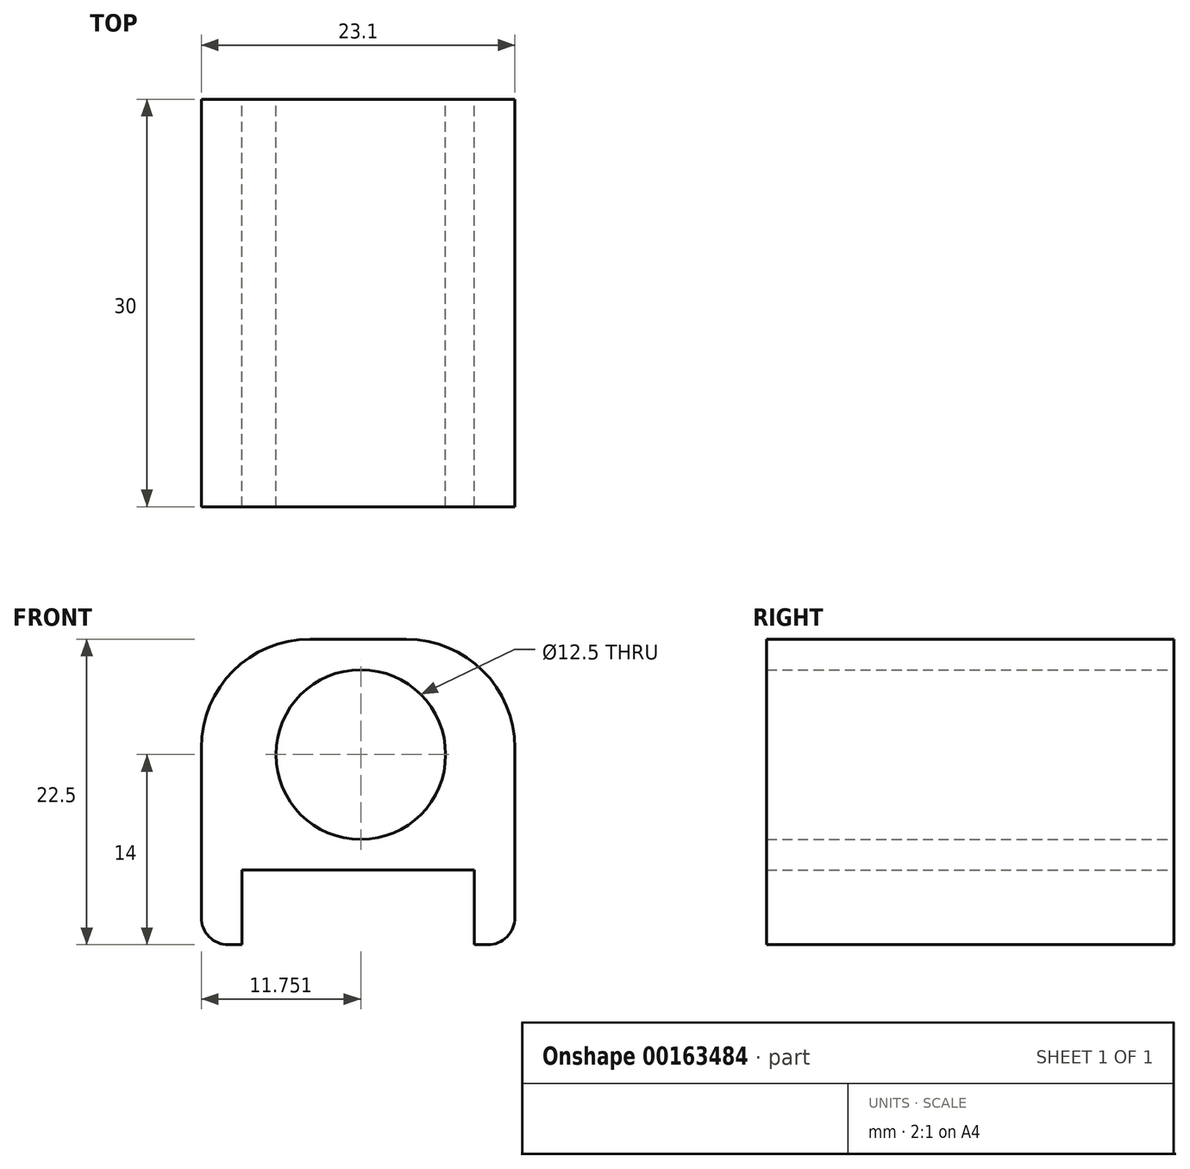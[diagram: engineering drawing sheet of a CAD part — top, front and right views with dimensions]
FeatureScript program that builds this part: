
annotation { "Feature Type Name" : "Feature", "Feature Type Description" : "" }
export const myFeature = defineFeature(function(context is Context, id is Id, definition is map)
    precondition{}
    {
        {
            var Q0;
            Q0=qCreatedBy(makeId("Front.planeOp"),FACE);
            var sketch = newSketch(context, id + "F0", { "sketchPlane" : qUnion([Q0])});
            skLineSegment(sketch, "E0.bottom", {"start": v(-11.26, 17) * mm, "end": v(-4.16, 17) * mm});
            skLineSegment(sketch, "E0.top", {"start": v(-19.26, 0) * mm, "end": v(3.84, 0) * mm});
            skLineSegment(sketch, "E0.left", {"start": v(-19.26, 9) * mm, "end": v(-19.26, 0) * mm});
            skLineSegment(sketch, "E0.right", {"start": v(3.84, 9) * mm, "end": v(3.84, 0) * mm});
            skLineSegment(sketch, "E1.bottom", {"start": v(-19.26, 0) * mm, "end": v(-16.26, 0) * mm});
            skLineSegment(sketch, "E1.top", {"start": v(-17.26, -5.5) * mm, "end": v(-16.26, -5.5) * mm});
            skLineSegment(sketch, "E1.left", {"start": v(-19.26, 0) * mm, "end": v(-19.26, -3.5) * mm});
            skLineSegment(sketch, "E1.right", {"start": v(-16.26, 0) * mm, "end": v(-16.26, -5.5) * mm});
            skLineSegment(sketch, "E2.bottom", {"start": v(3.84, 0) * mm, "end": v(0.84, 0) * mm});
            skLineSegment(sketch, "E2.top", {"start": v(1.84, -5.5) * mm, "end": v(0.84, -5.5) * mm});
            skLineSegment(sketch, "E2.left", {"start": v(3.84, 0) * mm, "end": v(3.84, -3.5) * mm});
            skLineSegment(sketch, "E2.right", {"start": v(0.84, 0) * mm, "end": v(0.84, -5.5) * mm});
            skCircle(sketch, "E3", {"center": v(-7.5, 8.5) * mm, "radius": 6.25 * mm});
            skPoint(sketch, "E3.centerSnap0", {"position": v(-19.26, 8.5) * mm});
            skPoint(sketch, "E4.visualSharp", {"position": v(-19.26, 17) * mm});
            skArc(sketch, "E4.filletArc", {"start": v(-11.26, 17) * mm, "mid": v(-16.92, 14.66) * mm, "end": v(-19.26, 9) * mm});
            skPoint(sketch, "E5.visualSharp", {"position": v(3.84, 17) * mm});
            skArc(sketch, "E5.filletArc", {"start": v(3.84, 9) * mm, "mid": v(1.5, 14.66) * mm, "end": v(-4.16, 17) * mm});
            skPoint(sketch, "E6.visualSharp", {"position": v(-19.26, -5.5) * mm});
            skArc(sketch, "E6.filletArc", {"start": v(-19.26, -3.5) * mm, "mid": v(-18.67, -4.91) * mm, "end": v(-17.26, -5.5) * mm});
            skPoint(sketch, "E7.visualSharp", {"position": v(3.84, -5.5) * mm});
            skArc(sketch, "E7.filletArc", {"start": v(1.84, -5.5) * mm, "mid": v(3.25, -4.91) * mm, "end": v(3.84, -3.5) * mm});
            skSolve(sketch);
        }
        {
            var Q0;
            Q0 = qSketchRegion(id + "F0", true);
            var Q1;
            Q1=makeQuery(id+"F0.imprint","IMPRINT",FACE,{"disambiguationData":[TD([[makeQuery(id+"F0.imprint","IMPRINT",EDGE,{"derivedFrom":sQuery(id+"F0.wireOp",EDGE,"E0.bottom")}),-1.0]])]});
            extrude(context, id + "F1", {"entities" : qUnion([Q0, Q1]), "depth" : 30 * mm});
        }
    });
